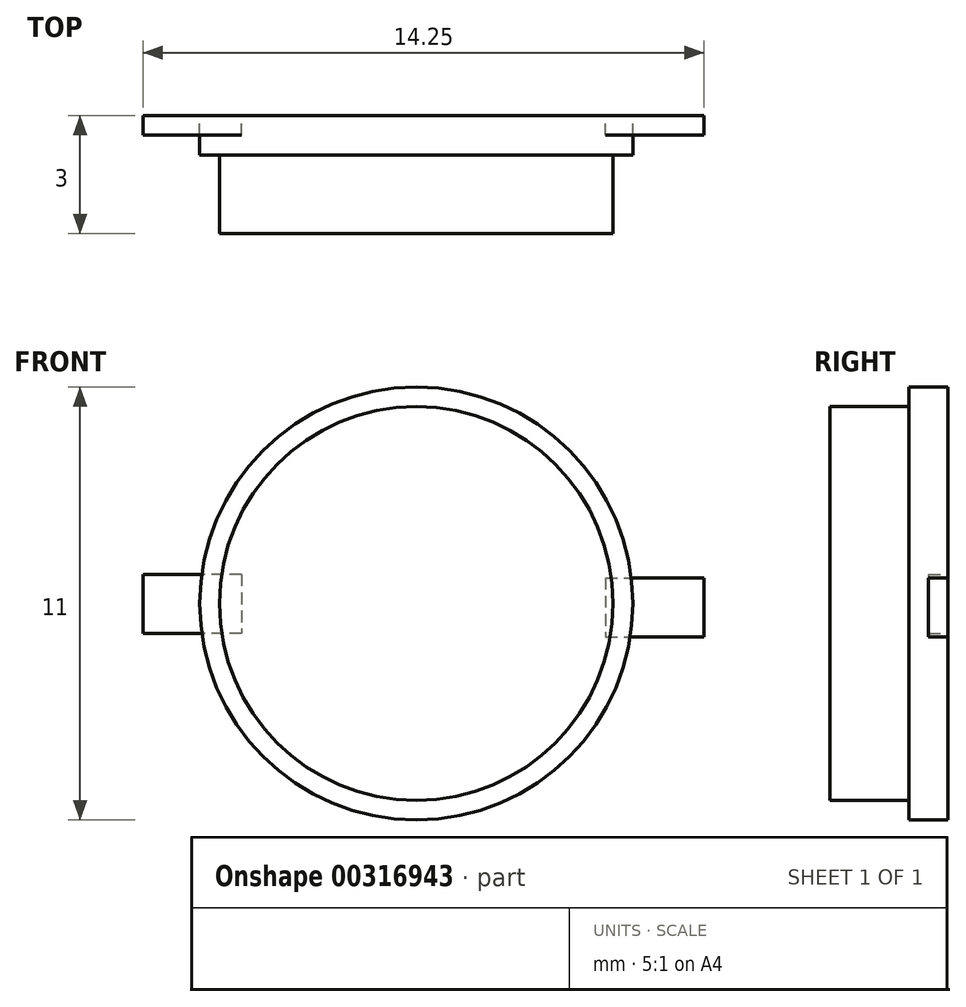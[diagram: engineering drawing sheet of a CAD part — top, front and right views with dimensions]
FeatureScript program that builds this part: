
annotation { "Feature Type Name" : "Feature", "Feature Type Description" : "" }
export const myFeature = defineFeature(function(context is Context, id is Id, definition is map)
    precondition{}
    {
        {
            var Q0;
            Q0=qCreatedBy(makeId("Front.planeOp"),FACE);
            var sketch = newSketch(context, id + "F0", { "sketchPlane" : qUnion([Q0])});
            skCircle(sketch, "E0", {"center": v(0, 0) * mm, "radius": 5.5 * mm});
            skSolve(sketch);
        }
        {
            var Q0;
            Q0=makeQuery(id+"F0.imprint","IMPRINT",FACE,{"disambiguationData":[TD([[makeQuery(id+"F0.imprint","IMPRINT",EDGE,{"derivedFrom":sQuery(id+"F0.wireOp",EDGE,"E0")}),1.0]])]});
            extrude(context, id + "F1", {"entities" : qUnion([Q0]), "depth" : 1 * mm});
        }
        {
            var Q0;
            Q0=makeQuery(id+"F1.opExtrude","CAP_FACE",FACE,{"disambiguationData":[OSD([sQuery(id+"F0.wireOp",EDGE,"E0")])],"isStart":false});
            var sketch = newSketch(context, id + "F2", { "sketchPlane" : qUnion([Q0])});
            skCircle(sketch, "E1", {"center": v(0, 0) * mm, "radius": 5 * mm});
            skSolve(sketch);
        }
        {
            var Q0;
            Q0=makeQuery(id+"F2.imprint","IMPRINT",FACE,{"disambiguationData":[TD([[makeQuery(id+"F2.imprint","IMPRINT",EDGE,{"derivedFrom":sQuery(id+"F2.wireOp",EDGE,"E1")}),1.0]])]});
            extrude(context, id + "F3", {"entities" : qUnion([Q0]), "operationType" : NewBodyOperationType.ADD, "depth" : 2 * mm});
        }
        {
            var Q0;
            Q0=qCreatedBy(makeId("Front.planeOp"),FACE);
            var sketch = newSketch(context, id + "F4", { "sketchPlane" : qUnion([Q0])});
            skLineSegment(sketch, "E2.bottom", {"start": v(4.81, 0.66) * mm, "end": v(7.31, 0.66) * mm});
            skLineSegment(sketch, "E2.top", {"start": v(4.81, -0.84) * mm, "end": v(7.31, -0.84) * mm});
            skLineSegment(sketch, "E2.left", {"start": v(4.81, 0.66) * mm, "end": v(4.81, -0.84) * mm});
            skLineSegment(sketch, "E2.right", {"start": v(7.31, 0.66) * mm, "end": v(7.31, -0.84) * mm});
            skSolve(sketch);
        }
        {
            var Q0;
            Q0=qCreatedBy(makeId("Front.planeOp"),FACE);
            var sketch = newSketch(context, id + "F5", { "sketchPlane" : qUnion([Q0])});
            skLineSegment(sketch, "E3.bottom", {"start": v(-4.44, 0.74) * mm, "end": v(-6.94, 0.74) * mm});
            skLineSegment(sketch, "E3.top", {"start": v(-4.44, -0.76) * mm, "end": v(-6.94, -0.76) * mm});
            skLineSegment(sketch, "E3.left", {"start": v(-4.44, 0.74) * mm, "end": v(-4.44, -0.76) * mm});
            skLineSegment(sketch, "E3.right", {"start": v(-6.94, 0.74) * mm, "end": v(-6.94, -0.76) * mm});
            skSolve(sketch);
        }
        {
            var Q0;
            Q0=makeQuery(id+"F4.imprint","IMPRINT",FACE,{"disambiguationData":[TD([[makeQuery(id+"F4.imprint","IMPRINT",EDGE,{"derivedFrom":sQuery(id+"F4.wireOp",EDGE,"E2.bottom")}),-1.0]])]});
            extrude(context, id + "F6", {"entities" : qUnion([Q0]), "depth" : 0.5 * mm});
        }
        {
            var Q0;
            Q0=makeQuery(id+"F5.imprint","IMPRINT",FACE,{"disambiguationData":[TD([[makeQuery(id+"F5.imprint","IMPRINT",EDGE,{"derivedFrom":sQuery(id+"F5.wireOp",EDGE,"E3.bottom")}),1.0]])]});
            extrude(context, id + "F7", {"entities" : qUnion([Q0]), "depth" : 0.5 * mm});
        }
    });
